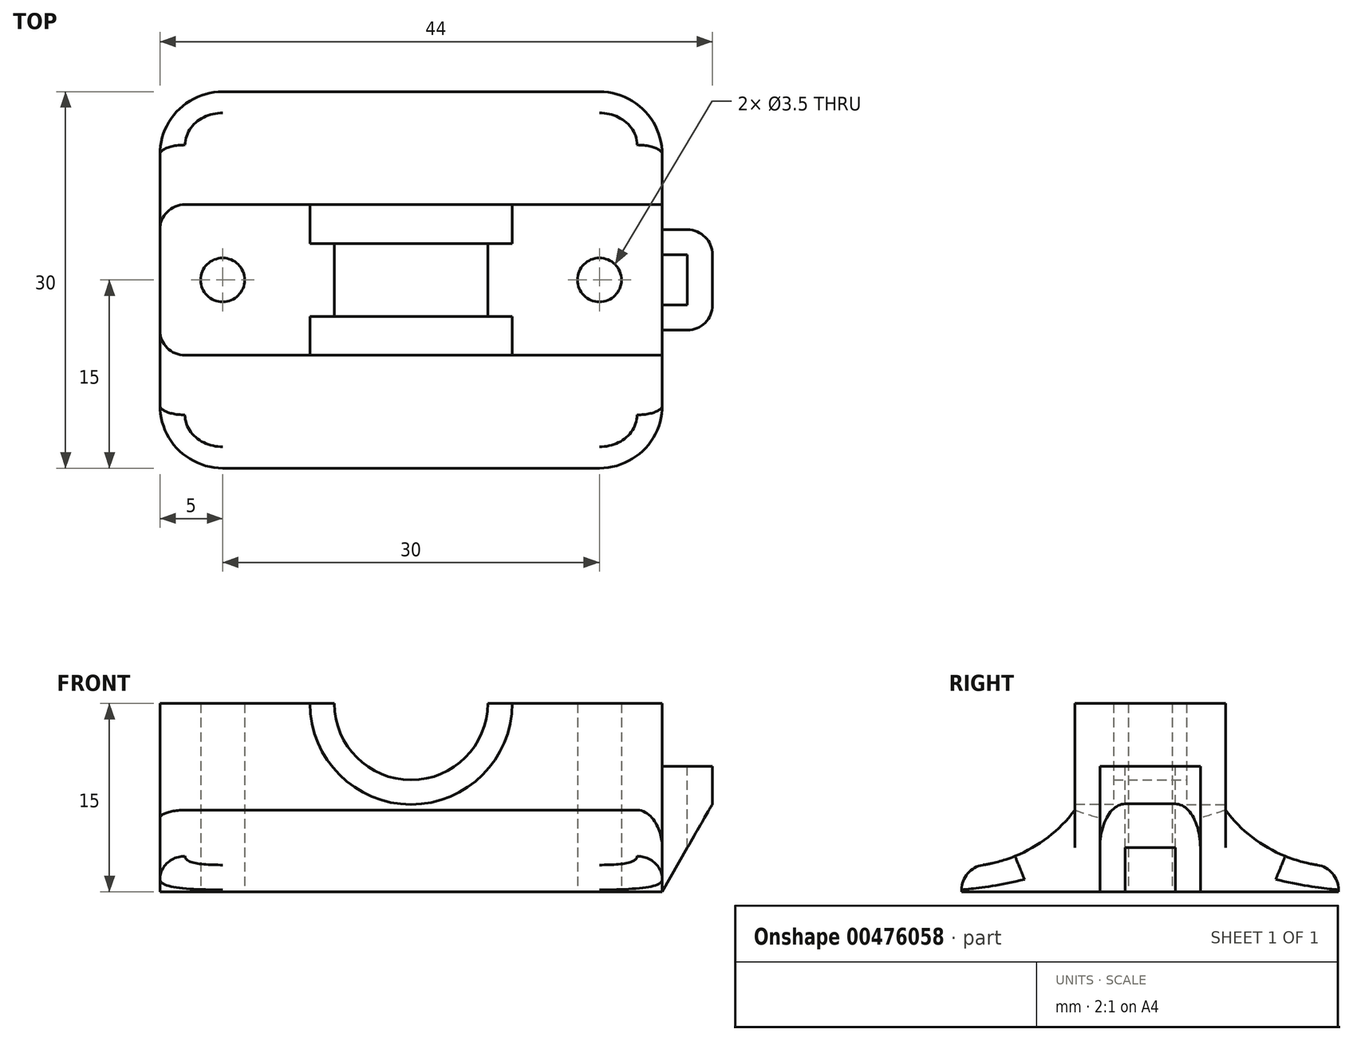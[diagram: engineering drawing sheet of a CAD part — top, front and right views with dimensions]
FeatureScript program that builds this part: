
annotation { "Feature Type Name" : "Feature", "Feature Type Description" : "" }
export const myFeature = defineFeature(function(context is Context, id is Id, definition is map)
    precondition{}
    {
        {
            var Q0;
            Q0=qCreatedBy(makeId("Front.planeOp"),FACE);
            var sketch = newSketch(context, id + "F0", { "sketchPlane" : qUnion([Q0])});
            skLineSegment(sketch, "E0.bottom", {"start": v(-20, 15) * mm, "end": v(-6.1, 15) * mm});
            skLineSegment(sketch, "E0.top", {"start": v(-20, 0) * mm, "end": v(20, 0) * mm});
            skLineSegment(sketch, "E0.left", {"start": v(-20, 15) * mm, "end": v(-20, 0) * mm});
            skLineSegment(sketch, "E0.right", {"start": v(20, 15) * mm, "end": v(20, 0) * mm});
            skArc(sketch, "E1", {"start": v(-6.1, 15) * mm, "mid": v(0, 8.9) * mm, "end": v(6.1, 15) * mm});
            skLineSegment(sketch, "E2.trimOffspring", {"start": v(6.1, 15) * mm, "end": v(20, 15) * mm});
            skSolve(sketch);
        }
        {
            var Q0;
            Q0 = qSketchRegion(id + "F0", true);
            extrude(context, id + "F1", {"entities" : qUnion([Q0]), "depth" : 15 * mm, "hasSecondDirection" : true, "secondDirectionOppositeDirection" : true, "secondDirectionDepth" : 15 * mm});
        }
        {
            var Q0;
            Q0=makeQuery(id+"F1.opExtrude","SWEPT_FACE",FACE,{"disambiguationData":[OSD([sQuery(id+"F0.wireOp",EDGE,"E0.right")])]});
            var sketch = newSketch(context, id + "F2", { "sketchPlane" : qUnion([Q0])});
            skLineSegment(sketch, "E3", {"start": v(-6, 15) * mm, "end": v(0, 15) * mm, "construction": true});
            skLineSegment(sketch, "E4", {"start": v(-26.87, 2) * mm, "end": v(22.7, 2) * mm, "construction": true});
            skLineSegment(sketch, "E5", {"start": v(-15, 15) * mm, "end": v(-15, -3.58) * mm});
            skLineSegment(sketch, "E6.MirrorCS", {"start": v(15, 15) * mm, "end": v(15, -3.58) * mm});
            skLineSegment(sketch, "E7", {"start": v(-15, 15) * mm, "end": v(-6, 15) * mm});
            skLineSegment(sketch, "E8.MirrorCS", {"start": v(15, 15) * mm, "end": v(6, 15) * mm});
            skLineSegment(sketch, "E9", {"start": v(6, 15) * mm, "end": v(6, 6.5) * mm});
            skArc(sketch, "E10", {"start": v(6, 6.5) * mm, "mid": v(9.97, 3.19) * mm, "end": v(15, 2) * mm});
            skLineSegment(sketch, "E11.MirrorCS", {"start": v(-6, 15) * mm, "end": v(-6, 6.5) * mm});
            skArc(sketch, "E12.MirrorCS", {"start": v(-6, 6.5) * mm, "mid": v(-9.97, 3.19) * mm, "end": v(-15, 2) * mm});
            skSolve(sketch);
        }
        {
            var Q0;
            Q0 = qSketchRegion(id + "F2", true);
            extrude(context, id + "F3", {"entities" : qUnion([Q0]), "operationType" : NewBodyOperationType.REMOVE, "endBound" : BoundingType.THROUGH_ALL, "oppositeDirection" : true, "depth" : 25 * mm});
        }
        {
            var Q0;
            Q0 = qSketchRegion(id + "F2", true);
            extrude(context, id + "F4", {"entities" : qUnion([Q0]), "operationType" : NewBodyOperationType.REMOVE, "endBound" : BoundingType.THROUGH_ALL, "oppositeDirection" : true, "depth" : 25 * mm});
        }
        {
            var Q0;
            Q0=makeQuery(id+"F1.opExtrude","SWEPT_FACE",FACE,{"disambiguationData":[OSD([sQuery(id+"F0.wireOp",EDGE,"E0.top")])]});
            var sketch = newSketch(context, id + "F5", { "sketchPlane" : qUnion([Q0])});
            skCircle(sketch, "E13", {"center": v(15, 0) * mm, "radius": 1.75 * mm});
            skCircle(sketch, "E14.MirrorC", {"center": v(-15, 0) * mm, "radius": 1.75 * mm});
            skSolve(sketch);
        }
        {
            var Q0;
            Q0 = qSketchRegion(id + "F5", true);
            extrude(context, id + "F6", {"entities" : qUnion([Q0]), "operationType" : NewBodyOperationType.REMOVE, "endBound" : BoundingType.THROUGH_ALL, "oppositeDirection" : true, "depth" : 25 * mm});
        }
        {
            var Q0;
            Q0=makeQuery(id+"F1.opExtrude","CAP_EDGE",EDGE,{"disambiguationData":[OSD([sQuery(id+"F0.wireOp",EDGE,"E0.right")])],"isStart":true});
            var Q1;
            Q1=makeQuery(id+"F1.opExtrude","CAP_EDGE",EDGE,{"disambiguationData":[OSD([sQuery(id+"F0.wireOp",EDGE,"E0.right")])],"isStart":false});
            var Q2;
            Q2=makeQuery(id+"F1.opExtrude","CAP_EDGE",EDGE,{"disambiguationData":[OSD([sQuery(id+"F0.wireOp",EDGE,"E0.left")])],"isStart":false});
            var Q3;
            Q3=makeQuery(id+"F1.opExtrude","CAP_EDGE",EDGE,{"disambiguationData":[OSD([sQuery(id+"F0.wireOp",EDGE,"E0.left")])],"isStart":true});
            fillet(context, id + "F7", {"entities" : qUnion([Q0, Q1, Q2, Q3]), "radius" : 5 * mm, "tangentPropagation" : true, "allowEdgeOverflow" : false});
        }
        {
            var Q0;
            Q0=makeQuery(id+"F3.boolean.opBoolean","INTERSECT",EDGE,{"derivedFrom":[makeQuery(id+"F1.opExtrude","SWEPT_FACE",FACE,{"disambiguationData":[OSD([sQuery(id+"F0.wireOp",EDGE,"E0.left")])]}),makeQuery(id+"F3.opExtrude","SWEPT_FACE",FACE,{"disambiguationData":[OSD([sQuery(id+"F2.wireOp",EDGE,"E10")])]})]});
            var Q1;
            Q1=makeQuery(id+"F3.boolean.opBoolean","INTERSECT",EDGE,{"derivedFrom":[makeQuery(id+"F1.opExtrude","SWEPT_FACE",FACE,{"disambiguationData":[OSD([sQuery(id+"F0.wireOp",EDGE,"E0.left")])]}),makeQuery(id+"F3.opExtrude","SWEPT_FACE",FACE,{"disambiguationData":[OSD([sQuery(id+"F2.wireOp",EDGE,"E9")])]})]});
            var Q2;
            Q2=makeQuery(id+"F3.boolean.opBoolean","COPY",EDGE,{"derivedFrom":makeQuery(id+"F3.opExtrude","CAP_EDGE",EDGE,{"disambiguationData":[OSD([sQuery(id+"F2.wireOp",EDGE,"E10")])],"isStart":true})});
            var Q3;
            Q3=makeQuery(id+"F3.boolean.opBoolean","COPY",EDGE,{"derivedFrom":makeQuery(id+"F3.opExtrude","CAP_EDGE",EDGE,{"disambiguationData":[OSD([sQuery(id+"F2.wireOp",EDGE,"E9")])],"isStart":true})});
            var Q4;
            Q4=makeQuery(id+"F3.boolean.opBoolean","COPY",EDGE,{"derivedFrom":makeQuery(id+"F3.opExtrude","CAP_EDGE",EDGE,{"disambiguationData":[OSD([sQuery(id+"F2.wireOp",EDGE,"E12.MirrorCS")])],"isStart":true})});
            var Q5;
            Q5=makeQuery(id+"F3.boolean.opBoolean","COPY",EDGE,{"derivedFrom":makeQuery(id+"F3.opExtrude","CAP_EDGE",EDGE,{"disambiguationData":[OSD([sQuery(id+"F2.wireOp",EDGE,"E11.MirrorCS")])],"isStart":true})});
            var Q6;
            Q6=makeQuery(id+"F3.boolean.opBoolean","INTERSECT",EDGE,{"derivedFrom":[makeQuery(id+"F1.opExtrude","SWEPT_FACE",FACE,{"disambiguationData":[OSD([sQuery(id+"F0.wireOp",EDGE,"E0.left")])]}),makeQuery(id+"F3.opExtrude","SWEPT_FACE",FACE,{"disambiguationData":[OSD([sQuery(id+"F2.wireOp",EDGE,"E12.MirrorCS")])]})]});
            var Q7;
            Q7=makeQuery(id+"F3.boolean.opBoolean","INTERSECT",EDGE,{"derivedFrom":[makeQuery(id+"F1.opExtrude","SWEPT_FACE",FACE,{"disambiguationData":[OSD([sQuery(id+"F0.wireOp",EDGE,"E0.left")])]}),makeQuery(id+"F3.opExtrude","SWEPT_FACE",FACE,{"disambiguationData":[OSD([sQuery(id+"F2.wireOp",EDGE,"E11.MirrorCS")])]})]});
            var Q8;
            Q8=makeQuery(id+"F3.boolean.opBoolean","COPY",EDGE,{"derivedFrom":makeQuery(id+"F3.opExtrude","SWEPT_EDGE",EDGE,{"disambiguationData":[OSD([sQuery(id+"F2.wireOp",EDGE,"E5"),sQuery(id+"F2.wireOp",EDGE,"E12.MirrorCS")])]})});
            var Q9;
            Q9=makeQuery(id+"F3.boolean.opBoolean","COPY",EDGE,{"derivedFrom":makeQuery(id+"F3.opExtrude","SWEPT_EDGE",EDGE,{"disambiguationData":[OSD([sQuery(id+"F2.wireOp",EDGE,"E6.MirrorCS"),sQuery(id+"F2.wireOp",EDGE,"E10")])]})});
            fillet(context, id + "F8", {"entities" : qUnion([Q0, Q1, Q2, Q3, Q4, Q5, Q6, Q7, Q8, Q9]), "radius" : 2 * mm, "tangentPropagation" : true, "allowEdgeOverflow" : false});
        }
        {
            var Q0;
            Q0=makeQuery(id+"F3.boolean.opBoolean","COPY",FACE,{"derivedFrom":makeQuery(id+"F3.opExtrude","SWEPT_FACE",FACE,{"disambiguationData":[OSD([sQuery(id+"F2.wireOp",EDGE,"E9")])]})});
            var sketch = newSketch(context, id + "F9", { "sketchPlane" : qUnion([Q0])});
            skCircle(sketch, "E15", {"center": v(0, 15) * mm, "radius": 8.05 * mm});
            skSolve(sketch);
        }
        {
            var Q0;
            Q0 = qSketchRegion(id + "F9", true);
            extrude(context, id + "F10", {"entities" : qUnion([Q0]), "operationType" : NewBodyOperationType.REMOVE, "oppositeDirection" : true, "depth" : 3.1 * mm});
        }
        {
            var Q0;
            Q0=makeQuery(id+"F3.boolean.opBoolean","COPY",FACE,{"derivedFrom":makeQuery(id+"F3.opExtrude","SWEPT_FACE",FACE,{"disambiguationData":[OSD([sQuery(id+"F2.wireOp",EDGE,"E11.MirrorCS")])]})});
            var sketch = newSketch(context, id + "F11", { "sketchPlane" : qUnion([Q0])});
            skCircle(sketch, "E16", {"center": v(0, 15) * mm, "radius": 8.05 * mm});
            skSolve(sketch);
        }
        {
            var Q0;
            Q0 = qSketchRegion(id + "F11", true);
            extrude(context, id + "F12", {"entities" : qUnion([Q0]), "operationType" : NewBodyOperationType.REMOVE, "oppositeDirection" : true, "depth" : 3.1 * mm});
        }
        {
            var Q0;
            Q0=makeQuery(id+"F1.opExtrude","SWEPT_FACE",FACE,{"disambiguationData":[OSD([sQuery(id+"F0.wireOp",EDGE,"E2.trimOffspring")])]});
            cPlane(context, id + "F13", {"entities" : qUnion([Q0]), "cplaneType" : CPlaneType.OFFSET, "offset" : 5 * mm, "oppositeDirection" : true, "width" : 150 * mm, "height" : 150 * mm});
        }
        {
            var Q0;
            Q0=qCreatedBy(id+"F13.planeOp",FACE);
            var sketch = newSketch(context, id + "F14", { "sketchPlane" : qUnion([Q0])});
            skLineSegment(sketch, "E17", {"start": v(24, -4) * mm, "end": v(24, 4) * mm});
            skLineSegment(sketch, "E18", {"start": v(24, 4) * mm, "end": v(20, 4) * mm});
            skLineSegment(sketch, "E19", {"start": v(20, -4) * mm, "end": v(24, -4) * mm});
            skLineSegment(sketch, "E20.bottom", {"start": v(20, 2) * mm, "end": v(22, 2) * mm});
            skLineSegment(sketch, "E20.top", {"start": v(20, -2) * mm, "end": v(22, -2) * mm});
            skLineSegment(sketch, "E20.right", {"start": v(22, 2) * mm, "end": v(22, -2) * mm});
            skLineSegment(sketch, "E21", {"start": v(20, 4) * mm, "end": v(20, 2) * mm});
            skLineSegment(sketch, "E22", {"start": v(20, -4) * mm, "end": v(20, -2) * mm});
            skSolve(sketch);
        }
        {
            var Q0;
            Q0 = qSketchRegion(id + "F14", true);
            extrude(context, id + "F15", {"entities" : qUnion([Q0]), "operationType" : NewBodyOperationType.ADD, "oppositeDirection" : true, "depth" : 10 * mm});
        }
        {
            var Q0;
            Q0=makeQuery(id+"F15.opExtrude","SWEPT_FACE",FACE,{"disambiguationData":[OSD([sQuery(id+"F14.wireOp",EDGE,"E19")])]});
            var sketch = newSketch(context, id + "F16", { "sketchPlane" : qUnion([Q0])});
            skLineSegment(sketch, "E23", {"start": v(20, 0) * mm, "end": v(24, 7) * mm});
            skLineSegment(sketch, "E24", {"start": v(24, 7) * mm, "end": v(24, 0) * mm});
            skLineSegment(sketch, "E25", {"start": v(24, 0) * mm, "end": v(20, 0) * mm});
            skSolve(sketch);
        }
        {
            var Q0;
            Q0 = qSketchRegion(id + "F16", true);
            extrude(context, id + "F17", {"entities" : qUnion([Q0]), "operationType" : NewBodyOperationType.REMOVE, "oppositeDirection" : true, "depth" : 25 * mm});
        }
        {
            var Q0;
            Q0=makeQuery(id+"F15.opExtrude","SWEPT_EDGE",EDGE,{"disambiguationData":[OSD([sQuery(id+"F14.wireOp",EDGE,"E17"),sQuery(id+"F14.wireOp",EDGE,"E18")])]});
            var Q1;
            Q1=makeQuery(id+"F15.opExtrude","SWEPT_EDGE",EDGE,{"disambiguationData":[OSD([sQuery(id+"F14.wireOp",EDGE,"E17"),sQuery(id+"F14.wireOp",EDGE,"E19")])]});
            fillet(context, id + "F18", {"entities" : qUnion([Q0, Q1]), "radius" : 2 * mm, "tangentPropagation" : true, "allowEdgeOverflow" : false});
        }
    });
